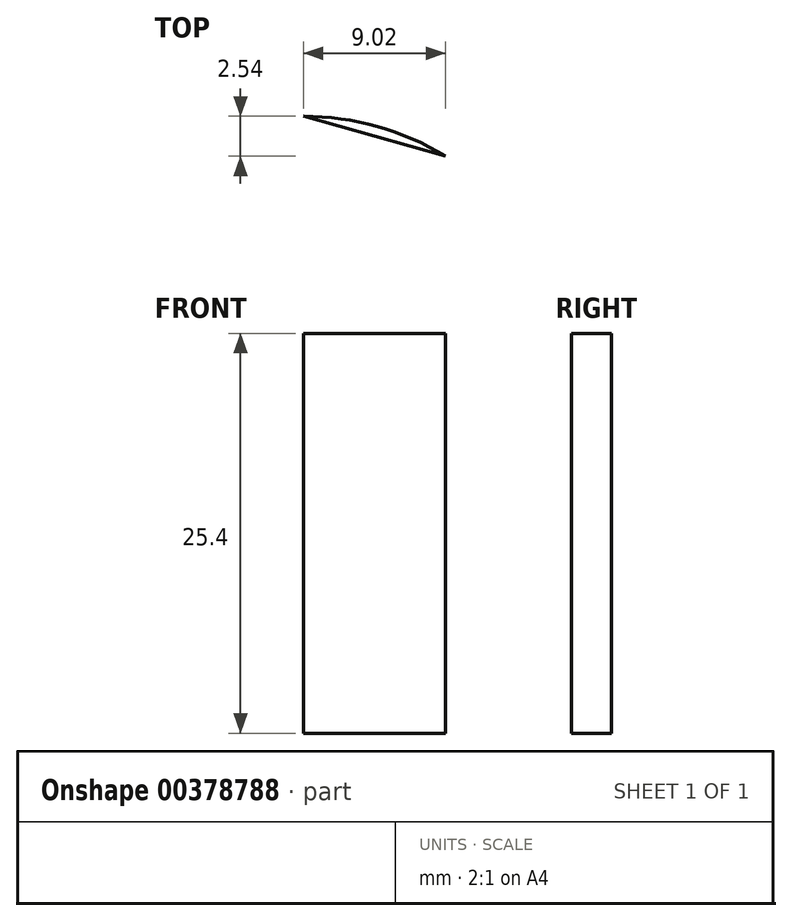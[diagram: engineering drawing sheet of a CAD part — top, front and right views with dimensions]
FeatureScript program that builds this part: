
annotation { "Feature Type Name" : "Feature", "Feature Type Description" : "" }
export const myFeature = defineFeature(function(context is Context, id is Id, definition is map)
    precondition{}
    {
        {
            var Q0;
            Q0=qCreatedBy(makeId("Top.planeOp"),FACE);
            var sketch = newSketch(context, id + "F0", { "sketchPlane" : qUnion([Q0])});
            skCircle(sketch, "E0", {"center": v(0, 0) * mm, "radius": 17.33 * mm});
            skCircle(sketch, "E1", {"center": v(45.43, 0) * mm, "radius": 4.4 * mm});
            skLineSegment(sketch, "E2", {"start": v(0, 17.33) * mm, "end": v(46.62, 4.24) * mm});
            skLineSegment(sketch, "E3", {"start": v(4.93, -16.61) * mm, "end": v(46.68, -4.22) * mm});
            skSolve(sketch);
        }
        {
            var Q0;
            {var subQ0=sQuery(id+"F0.wireOp",EDGE,"E2");var subQ1=sQuery(id+"F0.wireOp",EDGE,"E0");var subQ2=makeQuery(id+"F0.imprint","INTERSECT",VERTEX,{"disambiguationData":[OD(0.0)],"derivedFrom":[subQ1,subQ0]});Q0=makeQuery(id+"F0.imprint","IMPRINT",FACE,{"disambiguationData":[TD([[makeQuery(id+"F0.imprint","IMPRINT",EDGE,{"disambiguationData":[TD([[subQ2,-1.0]])],"derivedFrom":subQ1}),1.0]])]});}
            extrude(context, id + "F1", {"entities" : qUnion([Q0]), "depth" : 25.4 * mm});
        }
    });
